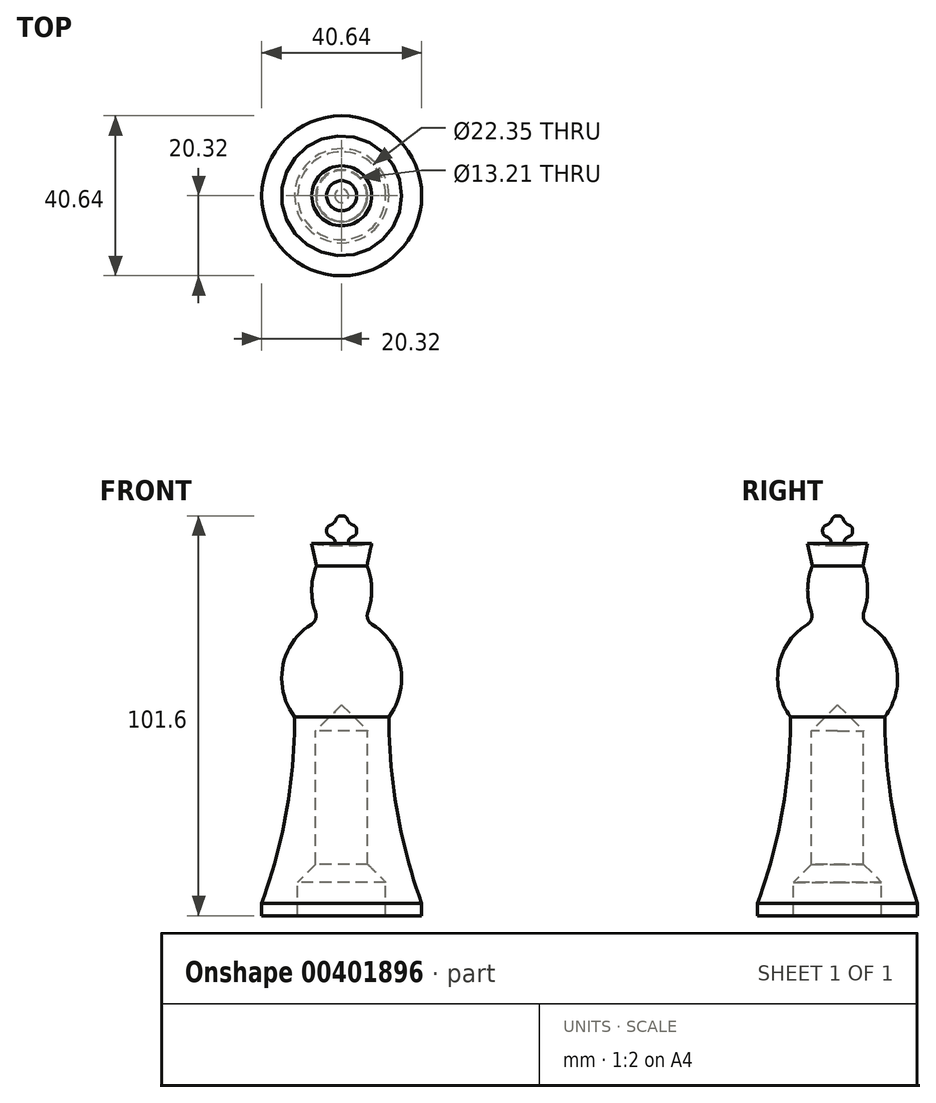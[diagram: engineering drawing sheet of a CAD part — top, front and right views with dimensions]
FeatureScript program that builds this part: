
annotation { "Feature Type Name" : "Feature", "Feature Type Description" : "" }
export const myFeature = defineFeature(function(context is Context, id is Id, definition is map)
    precondition{}
    {
        {
            var Q0;
            Q0=qCreatedBy(makeId("Front.planeOp"),FACE);
            var sketch = newSketch(context, id + "F0", { "sketchPlane" : qUnion([Q0])});
            skLineSegment(sketch, "E0", {"start": v(0, 0) * mm, "end": v(-11.18, 0) * mm, "construction": true});
            skLineSegment(sketch, "E1", {"start": v(-20.32, 0) * mm, "end": v(-20.32, 3.17) * mm});
            skLineSegment(sketch, "E2", {"start": v(0, 101.6) * mm, "end": v(0, 53.6) * mm});
            skLineSegment(sketch, "E3", {"start": v(0, 101.6) * mm, "end": v(-1.27, 101.6) * mm});
            skLineSegment(sketch, "E4", {"start": v(-1.27, 101.6) * mm, "end": v(-1.27, 99.06) * mm});
            skLineSegment(sketch, "E5", {"start": v(-1.27, 99.06) * mm, "end": v(-3.81, 99.06) * mm});
            skLineSegment(sketch, "E6", {"start": v(-3.8, 99.06) * mm, "end": v(-3.8, 96.52) * mm});
            skLineSegment(sketch, "E7", {"start": v(-3.81, 96.52) * mm, "end": v(-1.27, 96.52) * mm});
            skLineSegment(sketch, "E8", {"start": v(-1.27, 96.52) * mm, "end": v(-1.27, 93.98) * mm});
            skLineSegment(sketch, "E9", {"start": v(-20.32, 3.18) * mm, "end": v(-25.83, -11.97) * mm, "construction": true});
            skArc(sketch, "E10", {"start": v(-20.32, 3.18) * mm, "mid": v(-14.07, 26.49) * mm, "end": v(-11.97, 50.53) * mm});
            skEllipticalArc(sketch, "E11", {});
            skLineSegment(sketch, "E12", {"start": v(-6.4, 88.9) * mm, "end": v(-7.62, 94.62) * mm});
            skArc(sketch, "E13", {"start": v(-7.62, 94.61) * mm, "mid": v(-4.46, 94.18) * mm, "end": v(-1.27, 93.98) * mm});
            skEllipticalArc(sketch, "E14", {});
            skLineSegment(sketch, "E15", {"start": v(0, 53.6) * mm, "end": v(-6.6, 47) * mm});
            skLineSegment(sketch, "E16", {"start": v(-6.6, 47) * mm, "end": v(-6.6, 13.08) * mm});
            skLineSegment(sketch, "E17", {"start": v(-6.6, 13.08) * mm, "end": v(-11.18, 8.5) * mm});
            skLineSegment(sketch, "E18", {"start": v(-11.18, 8.5) * mm, "end": v(-11.18, 0) * mm});
            skLineSegment(sketch, "E19", {"start": v(0, 53.6) * mm, "end": v(0, 0) * mm, "construction": true});
            skLineSegment(sketch, "E20", {"start": v(-11.18, 0) * mm, "end": v(-20.32, 0) * mm});
            const initialGuessF0  = {"E11": [0, 0.08270986801319484, 0, 1, 0.01143, 0.00762, 0.9984029380380188, 2.3005239830219115], "E14": [0, 0.060358491469874126, -1, 0, 0.01524, 0.015875, 5.094282228583708, 0.6674388856346862]};
            skSetInitialGuess(sketch, initialGuessF0);
            skSolve(sketch);
        }
        {
            var Q0;
            Q0=makeQuery(id+"F0.imprint","IMPRINT",FACE,{"disambiguationData":[TD([[makeQuery(id+"F0.imprint","IMPRINT",EDGE,{"derivedFrom":sQuery(id+"F0.wireOp",EDGE,"E1")}),-1.0]])]});
            var Q1;
            Q1=sQuery(id+"F0.wireOp",EDGE,"E19");
            revolve(context, id + "F1", {"entities" : qUnion([Q0]), "axis" : qUnion([Q1]), "revolveType" : RevolveType.FULL});
        }
        {
            var Q0;
            Q0=makeQuery(id+"F1.opRevolve","SWEPT_EDGE",EDGE,{"disambiguationData":[OSD([sQuery(id+"F0.wireOp",EDGE,"E4"),sQuery(id+"F0.wireOp",EDGE,"E5")])]});
            var Q1;
            Q1=makeQuery(id+"F1.opRevolve","SWEPT_EDGE",EDGE,{"disambiguationData":[OSD([sQuery(id+"F0.wireOp",EDGE,"E7"),sQuery(id+"F0.wireOp",EDGE,"E8")])]});
            fillet(context, id + "F2", {"entities" : qUnion([Q0, Q1]), "radius" : 2.54 * mm, "tangentPropagation" : true, "allowEdgeOverflow" : false});
        }
        {
            var Q0;
            Q0=makeQuery(id+"F2.opFillet","BLEND_EDGE",EDGE,{"blendedFrom":[makeQuery(id+"F1.opRevolve","SWEPT_EDGE",EDGE,{"disambiguationData":[OSD([sQuery(id+"F0.wireOp",EDGE,"E4"),sQuery(id+"F0.wireOp",EDGE,"E5")])]}),makeQuery(id+"F1.opRevolve","SWEPT_FACE",FACE,{"disambiguationData":[OSD([sQuery(id+"F0.wireOp",EDGE,"E3")])]})],"blendedInto":[makeQuery(id+"F1.opRevolve","SWEPT_FACE",FACE,{"disambiguationData":[OSD([sQuery(id+"F0.wireOp",EDGE,"E3")])]})]});
            var Q1;
            Q1=makeQuery(id+"F2.opFillet","BLEND_EDGE",EDGE,{"blendedFrom":[makeQuery(id+"F1.opRevolve","SWEPT_EDGE",EDGE,{"disambiguationData":[OSD([sQuery(id+"F0.wireOp",EDGE,"E4"),sQuery(id+"F0.wireOp",EDGE,"E5")])]}),makeQuery(id+"F1.opRevolve","SWEPT_FACE",FACE,{"disambiguationData":[OSD([sQuery(id+"F0.wireOp",EDGE,"E6")])]})],"blendedInto":[makeQuery(id+"F1.opRevolve","SWEPT_FACE",FACE,{"disambiguationData":[OSD([sQuery(id+"F0.wireOp",EDGE,"E6")])]})]});
            var Q2;
            Q2=makeQuery(id+"F2.opFillet","BLEND_EDGE",EDGE,{"blendedFrom":[makeQuery(id+"F1.opRevolve","SWEPT_EDGE",EDGE,{"disambiguationData":[OSD([sQuery(id+"F0.wireOp",EDGE,"E7"),sQuery(id+"F0.wireOp",EDGE,"E8")])]}),makeQuery(id+"F1.opRevolve","SWEPT_FACE",FACE,{"disambiguationData":[OSD([sQuery(id+"F0.wireOp",EDGE,"E6")])]})],"blendedInto":[makeQuery(id+"F1.opRevolve","SWEPT_FACE",FACE,{"disambiguationData":[OSD([sQuery(id+"F0.wireOp",EDGE,"E6")])]})]});
            fillet(context, id + "F3", {"entities" : qUnion([Q0, Q1, Q2]), "radius" : 1.27 * mm, "tangentPropagation" : true, "allowEdgeOverflow" : false});
        }
        {
            var Q0;
            Q0=makeQuery(id+"F2.opFillet","BLEND_EDGE",EDGE,{"blendedFrom":[makeQuery(id+"F1.opRevolve","SWEPT_EDGE",EDGE,{"disambiguationData":[OSD([sQuery(id+"F0.wireOp",EDGE,"E7"),sQuery(id+"F0.wireOp",EDGE,"E8")])]}),makeQuery(id+"F1.opRevolve","SWEPT_FACE",FACE,{"disambiguationData":[OSD([sQuery(id+"F0.wireOp",EDGE,"E13")])]})],"blendedInto":[makeQuery(id+"F1.opRevolve","SWEPT_FACE",FACE,{"disambiguationData":[OSD([sQuery(id+"F0.wireOp",EDGE,"E13")])]})]});
            fillet(context, id + "F4", {"entities" : qUnion([Q0]), "radius" : 1.02 * mm, "tangentPropagation" : true, "allowEdgeOverflow" : false});
        }
        {
            var Q0;
            Q0=makeQuery(id+"F1.opRevolve","SWEPT_EDGE",EDGE,{"disambiguationData":[OSD([sQuery(id+"F0.wireOp",EDGE,"E11"),sQuery(id+"F0.wireOp",EDGE,"E14")])]});
            fillet(context, id + "F5", {"entities" : qUnion([Q0]), "radius" : 2.54 * mm, "tangentPropagation" : true, "allowEdgeOverflow" : false});
        }
    });
